# Revit family: IEK_Выключатель_Встраиваемый_10А трехклавишный IP20_ВЕГА
name_source: partatom
category: Выключатели
units: mm (PartAtom-declared; Revit-internal decimal feet)

## family parameters
Всегда вертикально = Да
На основе рабочей плоскости = Нет
Общий = Нет
При загрузке вырезать с полостями = Нет
Размер круглого соединителя = Использовать диаметр
Сохранять ориентацию аннотаций = Да
Тип детали = Нормальный
Точка расчета площади = Нет

## types (1)
- ВС10-3-0-ВБ
    ADSK_URL страницы изделия = https://www.iek.ru
    ADSK_Версия Revit = 2019
    ADSK_Версия семейства = 1.0
    ADSK_Группирование = III ЭЛЕКТРОУСТАНОВОЧНЫЕ И ЭЛЕКТРОМОНТАЖНЫЕ ИЗДЕЛИЯ
    ADSK_Единица измерения = шт
    ADSK_Завод-изготовитель = IEK
    ADSK_Код изделия = EVV30-K01-10-DM
    ADSK_Количество фаз = 1
    ADSK_Количество фаз числовое = 1
    ADSK_Марка = ВЕГА
    ADSK_Масса = 0.056
    ADSK_Материал = Цвет белый
    ADSK_Материал наименование = Пластик
    ADSK_Наименование = Выключатель 3-клавишный ВС10-3-0-ВБ 10А ВЕГА белый IEK
    ADSK_Напряжение = 220 В
    IEK_URL = https://www.iek.ru
    IEK_Описание = Серия «ВЕГА» включает в себя розетки и выключатели для скрытого монтажа, которые хорошо впишутся в любой интерьер квартир, загородных домов, офисных и производственных помещений.
    IEK_Цена за единицу = 141.22
    KSI_CMa_Строительные материалы = 01.7.14.03
    KSI_CPr_Строительные изделия = 20.4.01
    Высота = 81 мм
    Глубина = 36 мм
    Изготовитель = IEK
    Степень защиты = IP20
    Тип монтажа = Скрытый монтаж (в штукатурку)
    Ширина = 82 мм
